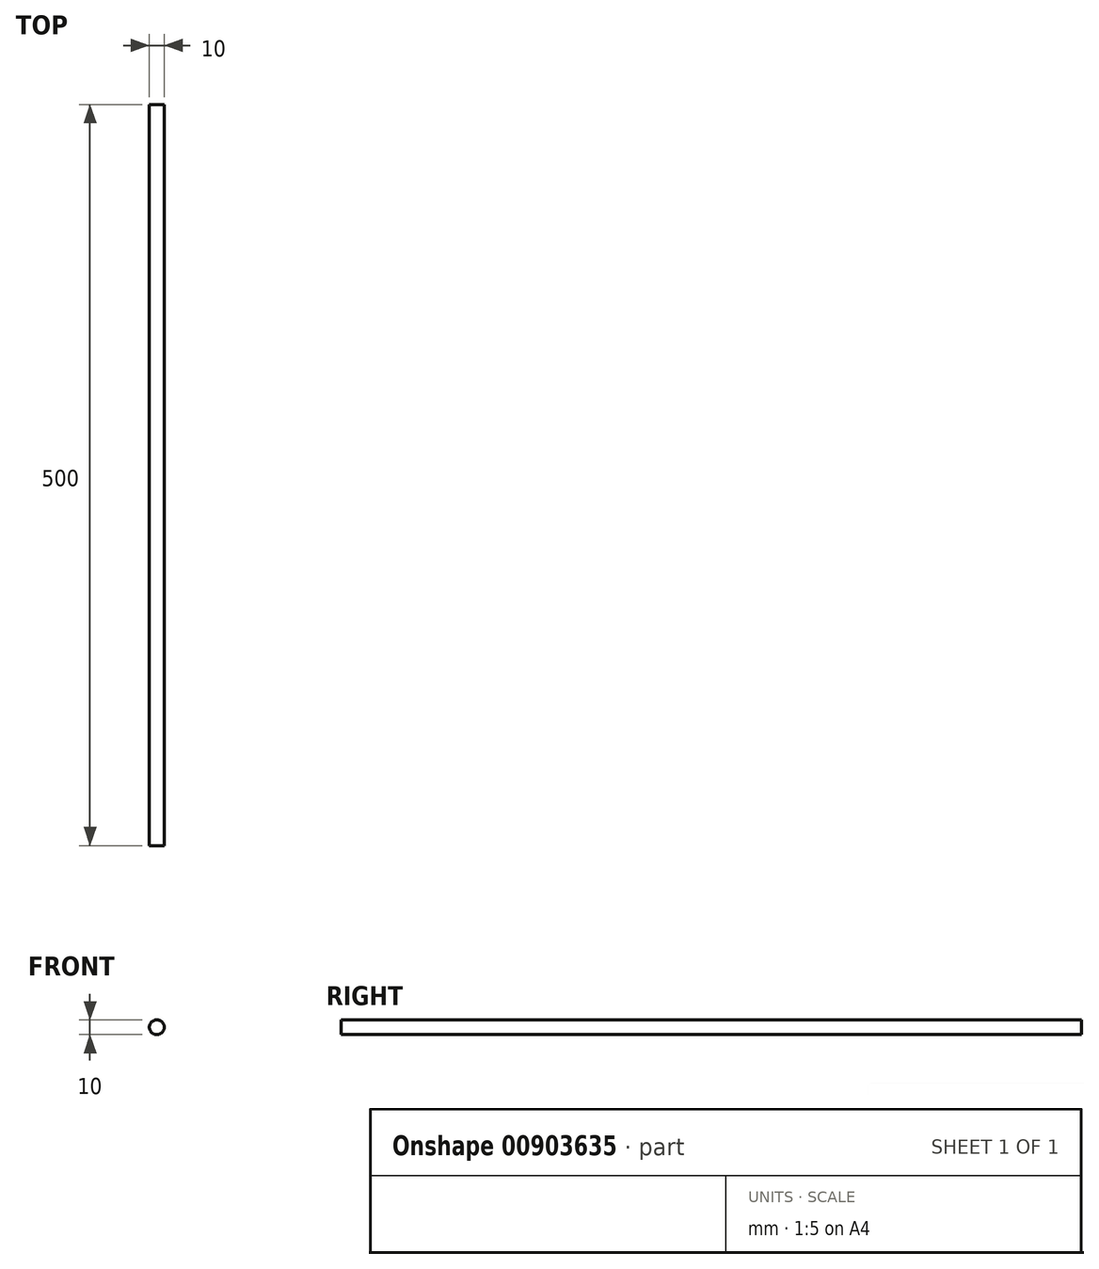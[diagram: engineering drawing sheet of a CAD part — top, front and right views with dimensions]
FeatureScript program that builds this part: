
annotation { "Feature Type Name" : "Feature", "Feature Type Description" : "" }
export const myFeature = defineFeature(function(context is Context, id is Id, definition is map)
    precondition{}
    {
        {
            var Q0;
            Q0=qCreatedBy(makeId("Front.planeOp"),FACE);
            var sketch = newSketch(context, id + "F0", { "sketchPlane" : qUnion([Q0])});
            skCircle(sketch, "E0", {"center": v(0, 0) * mm, "radius": 5 * mm});
            skSolve(sketch);
        }
        {
            var Q0;
            Q0=qSketchRegion(id+"F0",true);
            extrude(context, id + "F1", {"entities" : qUnion([Q0]), "depth" : 500 * mm, "offsetDistance" : 25.4 * mm});
        }
    });
